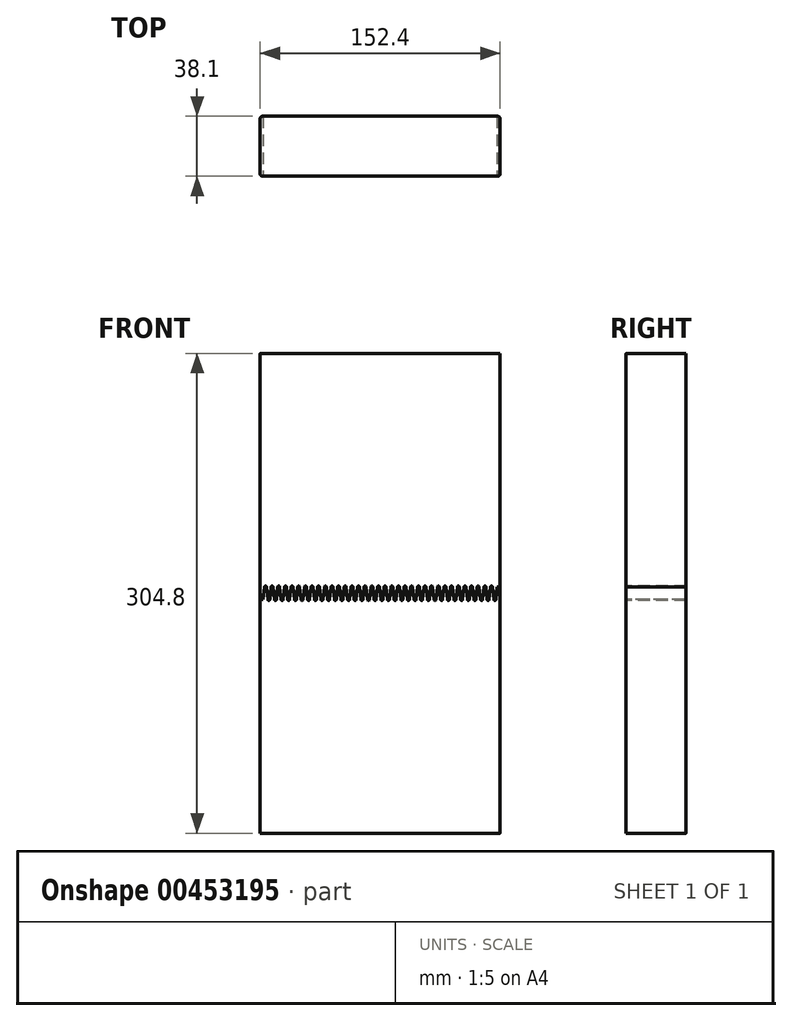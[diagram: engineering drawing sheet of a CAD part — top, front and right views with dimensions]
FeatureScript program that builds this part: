
annotation { "Feature Type Name" : "Feature", "Feature Type Description" : "" }
export const myFeature = defineFeature(function(context is Context, id is Id, definition is map)
    precondition{}
    {
        {
            var Q0;
            Q0=qCreatedBy(makeId("Front.planeOp"),FACE);
            var sketch = newSketch(context, id + "F0", { "sketchPlane" : qUnion([Q0])});
            skLineSegment(sketch, "E0.bottom", {"start": v(0, 0) * mm, "end": v(-152.4, 0) * mm});
            skLineSegment(sketch, "E0.top", {"start": v(0, 304.8) * mm, "end": v(-152.4, 304.8) * mm});
            skLineSegment(sketch, "E0.left", {"start": v(0, 0) * mm, "end": v(0, 304.8) * mm});
            skLineSegment(sketch, "E0.right", {"start": v(-152.4, 0) * mm, "end": v(-152.4, 304.8) * mm});
            skLineSegment(sketch, "E1", {"start": v(-152.4, 152.4) * mm, "end": v(0, 152.4) * mm, "construction": true});
            skArc(sketch, "E2.1.0.0", {"start": v(-148.4, 156.37) * mm, "mid": v(-149.03, 157) * mm, "end": v(-149.66, 156.37) * mm});
            skArc(sketch, "E2.2.0.0", {"start": v(-144.17, 156.37) * mm, "mid": v(-144.8, 157) * mm, "end": v(-145.44, 156.37) * mm});
            skLineSegment(sketch, "E2.direction1", {"start": v(-153.25, 156.37) * mm, "end": v(-152.14, 156.37) * mm, "construction": true});
            skArc(sketch, "E3.0.3.0", {"start": v(-139.95, 156.37) * mm, "mid": v(-140.58, 157) * mm, "end": v(-141.22, 156.37) * mm});
            skArc(sketch, "E3.0.4.0", {"start": v(-135.73, 156.37) * mm, "mid": v(-136.36, 157) * mm, "end": v(-137, 156.37) * mm});
            skArc(sketch, "E3.0.5.0", {"start": v(-131.5, 156.37) * mm, "mid": v(-132.14, 157) * mm, "end": v(-132.77, 156.37) * mm});
            skArc(sketch, "E3.0.6.0", {"start": v(-127.28, 156.37) * mm, "mid": v(-127.92, 157) * mm, "end": v(-128.55, 156.37) * mm});
            skArc(sketch, "E3.0.7.0", {"start": v(-123.06, 156.37) * mm, "mid": v(-123.7, 157) * mm, "end": v(-124.33, 156.37) * mm});
            skArc(sketch, "E3.0.8.0", {"start": v(-118.84, 156.37) * mm, "mid": v(-119.47, 157) * mm, "end": v(-120.1, 156.37) * mm});
            skArc(sketch, "E3.0.9.0", {"start": v(-114.61, 156.37) * mm, "mid": v(-115.25, 157) * mm, "end": v(-115.88, 156.37) * mm});
            skArc(sketch, "E3.0.10.0", {"start": v(-110.4, 156.37) * mm, "mid": v(-111.03, 157) * mm, "end": v(-111.66, 156.37) * mm});
            skArc(sketch, "E3.0.11.0", {"start": v(-106.17, 156.37) * mm, "mid": v(-106.8, 157) * mm, "end": v(-107.44, 156.37) * mm});
            skArc(sketch, "E3.0.12.0", {"start": v(-101.95, 156.37) * mm, "mid": v(-102.58, 157) * mm, "end": v(-103.22, 156.37) * mm});
            skArc(sketch, "E3.0.13.0", {"start": v(-97.72, 156.37) * mm, "mid": v(-98.36, 157) * mm, "end": v(-99, 156.37) * mm});
            skArc(sketch, "E3.0.14.0", {"start": v(-93.5, 156.37) * mm, "mid": v(-94.14, 157) * mm, "end": v(-94.77, 156.37) * mm});
            skArc(sketch, "E3.0.15.0", {"start": v(-89.28, 156.37) * mm, "mid": v(-89.91, 157) * mm, "end": v(-90.55, 156.37) * mm});
            skArc(sketch, "E3.0.16.0", {"start": v(-85.06, 156.37) * mm, "mid": v(-85.7, 157) * mm, "end": v(-86.33, 156.37) * mm});
            skArc(sketch, "E3.0.17.0", {"start": v(-80.83, 156.37) * mm, "mid": v(-81.47, 157) * mm, "end": v(-82.1, 156.37) * mm});
            skArc(sketch, "E3.0.18.0", {"start": v(-76.61, 156.37) * mm, "mid": v(-77.25, 157) * mm, "end": v(-77.88, 156.37) * mm});
            skArc(sketch, "E3.0.19.0", {"start": v(-72.39, 156.37) * mm, "mid": v(-73.02, 157) * mm, "end": v(-73.66, 156.37) * mm});
            skArc(sketch, "E3.0.20.0", {"start": v(-68.17, 156.37) * mm, "mid": v(-68.8, 157) * mm, "end": v(-69.44, 156.37) * mm});
            skArc(sketch, "E3.0.21.0", {"start": v(-63.94, 156.37) * mm, "mid": v(-64.58, 157) * mm, "end": v(-65.21, 156.37) * mm});
            skArc(sketch, "E3.0.22.0", {"start": v(-59.72, 156.37) * mm, "mid": v(-60.36, 157) * mm, "end": v(-61, 156.37) * mm});
            skArc(sketch, "E3.0.23.0", {"start": v(-55.5, 156.37) * mm, "mid": v(-56.13, 157) * mm, "end": v(-56.77, 156.37) * mm});
            skArc(sketch, "E3.0.24.0", {"start": v(-51.27, 156.37) * mm, "mid": v(-51.9, 157) * mm, "end": v(-52.54, 156.37) * mm});
            skArc(sketch, "E3.0.25.0", {"start": v(-47.05, 156.37) * mm, "mid": v(-47.69, 157) * mm, "end": v(-48.32, 156.37) * mm});
            skArc(sketch, "E3.0.26.0", {"start": v(-42.83, 156.37) * mm, "mid": v(-43.46, 157) * mm, "end": v(-44.1, 156.37) * mm});
            skArc(sketch, "E3.0.27.0", {"start": v(-38.6, 156.37) * mm, "mid": v(-39.24, 157) * mm, "end": v(-39.88, 156.37) * mm});
            skArc(sketch, "E3.0.28.0", {"start": v(-34.38, 156.37) * mm, "mid": v(-35.02, 157) * mm, "end": v(-35.65, 156.37) * mm});
            skArc(sketch, "E3.0.29.0", {"start": v(-30.16, 156.37) * mm, "mid": v(-30.8, 157) * mm, "end": v(-31.43, 156.37) * mm});
            skArc(sketch, "E4.0.30.0", {"start": v(-25.94, 156.37) * mm, "mid": v(-26.57, 157) * mm, "end": v(-27.2, 156.37) * mm});
            skArc(sketch, "E4.0.31.0", {"start": v(-21.72, 156.37) * mm, "mid": v(-22.35, 157) * mm, "end": v(-22.99, 156.37) * mm});
            skArc(sketch, "E4.0.32.0", {"start": v(-17.5, 156.37) * mm, "mid": v(-18.13, 157) * mm, "end": v(-18.76, 156.37) * mm});
            skArc(sketch, "E4.0.33.0", {"start": v(-13.27, 156.37) * mm, "mid": v(-13.87, 157) * mm, "end": v(-14.54, 156.44) * mm});
            skArc(sketch, "E4.0.34.0", {"start": v(-9.05, 156.37) * mm, "mid": v(-9.68, 157) * mm, "end": v(-10.32, 156.37) * mm});
            skArc(sketch, "E5.0.35.0", {"start": v(-4.83, 156.37) * mm, "mid": v(-5.46, 157) * mm, "end": v(-6.1, 156.37) * mm});
            skArc(sketch, "E6.1.0.0", {"start": v(-147.55, 148.43) * mm, "mid": v(-146.92, 147.8) * mm, "end": v(-146.28, 148.43) * mm});
            skArc(sketch, "E6.2.0.0", {"start": v(-143.33, 148.43) * mm, "mid": v(-142.7, 147.8) * mm, "end": v(-142.06, 148.43) * mm});
            skArc(sketch, "E6.3.0.0", {"start": v(-139.1, 148.43) * mm, "mid": v(-138.47, 147.8) * mm, "end": v(-137.84, 148.43) * mm});
            skArc(sketch, "E6.4.0.0", {"start": v(-134.88, 148.43) * mm, "mid": v(-134.25, 147.8) * mm, "end": v(-133.61, 148.43) * mm});
            skArc(sketch, "E6.5.0.0", {"start": v(-130.66, 148.43) * mm, "mid": v(-130.03, 147.8) * mm, "end": v(-129.4, 148.43) * mm});
            skArc(sketch, "E6.6.0.0", {"start": v(-126.44, 148.43) * mm, "mid": v(-125.8, 147.8) * mm, "end": v(-125.17, 148.43) * mm});
            skArc(sketch, "E6.7.0.0", {"start": v(-122.22, 148.43) * mm, "mid": v(-121.58, 147.8) * mm, "end": v(-120.95, 148.43) * mm});
            skArc(sketch, "E6.8.0.0", {"start": v(-118, 148.43) * mm, "mid": v(-117.36, 147.8) * mm, "end": v(-116.72, 148.43) * mm});
            skArc(sketch, "E6.9.0.0", {"start": v(-113.77, 148.43) * mm, "mid": v(-113.14, 147.8) * mm, "end": v(-112.5, 148.43) * mm});
            skArc(sketch, "E6.10.0.0", {"start": v(-109.55, 148.43) * mm, "mid": v(-108.91, 147.8) * mm, "end": v(-108.28, 148.43) * mm});
            skArc(sketch, "E6.11.0.0", {"start": v(-105.33, 148.43) * mm, "mid": v(-104.7, 147.8) * mm, "end": v(-104.06, 148.43) * mm});
            skArc(sketch, "E6.12.0.0", {"start": v(-101.1, 148.43) * mm, "mid": v(-100.47, 147.8) * mm, "end": v(-99.83, 148.43) * mm});
            skArc(sketch, "E6.13.0.0", {"start": v(-96.88, 148.43) * mm, "mid": v(-96.25, 147.8) * mm, "end": v(-95.61, 148.43) * mm});
            skArc(sketch, "E6.14.0.0", {"start": v(-92.66, 148.43) * mm, "mid": v(-92.02, 147.8) * mm, "end": v(-91.39, 148.43) * mm});
            skArc(sketch, "E6.15.0.0", {"start": v(-88.44, 148.43) * mm, "mid": v(-87.8, 147.8) * mm, "end": v(-87.17, 148.43) * mm});
            skArc(sketch, "E6.16.0.0", {"start": v(-84.21, 148.43) * mm, "mid": v(-83.58, 147.8) * mm, "end": v(-82.94, 148.43) * mm});
            skArc(sketch, "E6.17.0.0", {"start": v(-80, 148.43) * mm, "mid": v(-79.36, 147.8) * mm, "end": v(-78.72, 148.43) * mm});
            skArc(sketch, "E6.18.0.0", {"start": v(-75.77, 148.43) * mm, "mid": v(-75.13, 147.8) * mm, "end": v(-74.5, 148.43) * mm});
            skArc(sketch, "E6.19.0.0", {"start": v(-71.55, 148.43) * mm, "mid": v(-70.91, 147.8) * mm, "end": v(-70.28, 148.43) * mm});
            skArc(sketch, "E6.20.0.0", {"start": v(-67.32, 148.43) * mm, "mid": v(-66.69, 147.8) * mm, "end": v(-66.05, 148.43) * mm});
            skArc(sketch, "E6.21.0.0", {"start": v(-63.1, 148.43) * mm, "mid": v(-62.47, 147.8) * mm, "end": v(-61.83, 148.43) * mm});
            skArc(sketch, "E6.22.0.0", {"start": v(-58.88, 148.43) * mm, "mid": v(-58.24, 147.8) * mm, "end": v(-57.6, 148.43) * mm});
            skArc(sketch, "E6.23.0.0", {"start": v(-54.66, 148.43) * mm, "mid": v(-54.02, 147.8) * mm, "end": v(-53.39, 148.43) * mm});
            skArc(sketch, "E6.24.0.0", {"start": v(-50.43, 148.43) * mm, "mid": v(-49.8, 147.8) * mm, "end": v(-49.16, 148.43) * mm});
            skArc(sketch, "E6.25.0.0", {"start": v(-46.21, 148.43) * mm, "mid": v(-45.58, 147.8) * mm, "end": v(-44.94, 148.43) * mm});
            skArc(sketch, "E6.26.0.0", {"start": v(-41.99, 148.43) * mm, "mid": v(-41.35, 147.8) * mm, "end": v(-40.72, 148.43) * mm});
            skArc(sketch, "E6.27.0.0", {"start": v(-37.77, 148.43) * mm, "mid": v(-37.13, 147.8) * mm, "end": v(-36.5, 148.43) * mm});
            skArc(sketch, "E6.28.0.0", {"start": v(-33.54, 148.43) * mm, "mid": v(-32.9, 147.8) * mm, "end": v(-32.27, 148.43) * mm});
            skArc(sketch, "E6.29.0.0", {"start": v(-29.32, 148.43) * mm, "mid": v(-28.69, 147.8) * mm, "end": v(-28.05, 148.43) * mm});
            skArc(sketch, "E6.30.0.0", {"start": v(-25.1, 148.43) * mm, "mid": v(-24.46, 147.8) * mm, "end": v(-23.83, 148.43) * mm});
            skArc(sketch, "E6.31.0.0", {"start": v(-20.88, 148.43) * mm, "mid": v(-20.24, 147.8) * mm, "end": v(-19.6, 148.43) * mm});
            skArc(sketch, "E6.32.0.0", {"start": v(-16.65, 148.43) * mm, "mid": v(-16.02, 147.8) * mm, "end": v(-15.38, 148.43) * mm});
            skArc(sketch, "E6.33.0.0", {"start": v(-12.43, 148.43) * mm, "mid": v(-11.8, 147.8) * mm, "end": v(-11.16, 148.43) * mm});
            skArc(sketch, "E6.34.0.0", {"start": v(-8.2, 148.43) * mm, "mid": v(-7.57, 147.8) * mm, "end": v(-6.94, 148.43) * mm});
            skArc(sketch, "E6.35.0.0", {"start": v(-3.99, 148.43) * mm, "mid": v(-3.35, 147.8) * mm, "end": v(-2.72, 148.43) * mm});
            skLineSegment(sketch, "E7", {"start": v(-149.66, 156.44) * mm, "end": v(-150.5, 148.36) * mm});
            skLineSegment(sketch, "E8", {"start": v(-148.4, 156.44) * mm, "end": v(-147.55, 148.36) * mm});
            skLineSegment(sketch, "E9.1.0.0", {"start": v(-145.44, 156.44) * mm, "end": v(-146.29, 148.36) * mm});
            skLineSegment(sketch, "E9.2.0.0", {"start": v(-141.21, 156.44) * mm, "end": v(-142.06, 148.36) * mm});
            skLineSegment(sketch, "E9.3.0.0", {"start": v(-137, 156.44) * mm, "end": v(-137.84, 148.36) * mm});
            skLineSegment(sketch, "E9.4.0.0", {"start": v(-132.77, 156.44) * mm, "end": v(-133.62, 148.36) * mm});
            skLineSegment(sketch, "E9.5.0.0", {"start": v(-128.55, 156.44) * mm, "end": v(-129.4, 148.36) * mm});
            skLineSegment(sketch, "E9.6.0.0", {"start": v(-124.32, 156.44) * mm, "end": v(-125.17, 148.36) * mm});
            skLineSegment(sketch, "E9.7.0.0", {"start": v(-120.1, 156.44) * mm, "end": v(-120.95, 148.36) * mm});
            skLineSegment(sketch, "E9.8.0.0", {"start": v(-115.88, 156.44) * mm, "end": v(-116.73, 148.36) * mm});
            skLineSegment(sketch, "E9.9.0.0", {"start": v(-111.66, 156.44) * mm, "end": v(-112.5, 148.36) * mm});
            skLineSegment(sketch, "E9.10.0.0", {"start": v(-107.43, 156.44) * mm, "end": v(-108.28, 148.36) * mm});
            skLineSegment(sketch, "E9.11.0.0", {"start": v(-103.21, 156.44) * mm, "end": v(-104.06, 148.36) * mm});
            skLineSegment(sketch, "E9.12.0.0", {"start": v(-98.99, 156.44) * mm, "end": v(-99.84, 148.36) * mm});
            skLineSegment(sketch, "E9.13.0.0", {"start": v(-94.77, 156.44) * mm, "end": v(-95.61, 148.36) * mm});
            skLineSegment(sketch, "E9.14.0.0", {"start": v(-90.54, 156.44) * mm, "end": v(-91.4, 148.36) * mm});
            skLineSegment(sketch, "E9.15.0.0", {"start": v(-86.32, 156.44) * mm, "end": v(-87.17, 148.36) * mm});
            skLineSegment(sketch, "E9.16.0.0", {"start": v(-82.1, 156.44) * mm, "end": v(-82.95, 148.36) * mm});
            skLineSegment(sketch, "E9.17.0.0", {"start": v(-77.88, 156.44) * mm, "end": v(-78.72, 148.36) * mm});
            skLineSegment(sketch, "E9.18.0.0", {"start": v(-73.65, 156.44) * mm, "end": v(-74.5, 148.36) * mm});
            skLineSegment(sketch, "E9.19.0.0", {"start": v(-69.43, 156.44) * mm, "end": v(-70.28, 148.36) * mm});
            skLineSegment(sketch, "E9.20.0.0", {"start": v(-65.2, 156.44) * mm, "end": v(-66.06, 148.36) * mm});
            skLineSegment(sketch, "E9.21.0.0", {"start": v(-60.99, 156.44) * mm, "end": v(-61.83, 148.36) * mm});
            skLineSegment(sketch, "E9.22.0.0", {"start": v(-56.76, 156.44) * mm, "end": v(-57.61, 148.36) * mm});
            skLineSegment(sketch, "E9.23.0.0", {"start": v(-52.54, 156.44) * mm, "end": v(-53.39, 148.36) * mm});
            skLineSegment(sketch, "E9.24.0.0", {"start": v(-48.32, 156.44) * mm, "end": v(-49.17, 148.36) * mm});
            skLineSegment(sketch, "E9.25.0.0", {"start": v(-44.1, 156.44) * mm, "end": v(-44.94, 148.36) * mm});
            skLineSegment(sketch, "E9.26.0.0", {"start": v(-39.87, 156.44) * mm, "end": v(-40.72, 148.36) * mm});
            skLineSegment(sketch, "E9.27.0.0", {"start": v(-35.65, 156.44) * mm, "end": v(-36.5, 148.36) * mm});
            skLineSegment(sketch, "E9.28.0.0", {"start": v(-31.43, 156.44) * mm, "end": v(-32.28, 148.36) * mm});
            skLineSegment(sketch, "E9.29.0.0", {"start": v(-27.2, 156.44) * mm, "end": v(-28.05, 148.36) * mm});
            skLineSegment(sketch, "E9.30.0.0", {"start": v(-22.98, 156.44) * mm, "end": v(-23.83, 148.36) * mm});
            skLineSegment(sketch, "E9.31.0.0", {"start": v(-18.76, 156.44) * mm, "end": v(-19.6, 148.36) * mm});
            skLineSegment(sketch, "E9.32.0.0", {"start": v(-14.54, 156.44) * mm, "end": v(-15.39, 148.36) * mm});
            skLineSegment(sketch, "E9.33.0.0", {"start": v(-10.32, 156.44) * mm, "end": v(-11.16, 148.36) * mm});
            skLineSegment(sketch, "E9.34.0.0", {"start": v(-6.1, 156.44) * mm, "end": v(-6.94, 148.36) * mm});
            skLineSegment(sketch, "E9.35.0.0", {"start": v(-1.87, 156.44) * mm, "end": v(-2.72, 148.36) * mm});
            skLineSegment(sketch, "E10.1.0.0", {"start": v(-144.17, 156.44) * mm, "end": v(-143.33, 148.36) * mm});
            skLineSegment(sketch, "E10.2.0.0", {"start": v(-139.95, 156.44) * mm, "end": v(-139.1, 148.36) * mm});
            skLineSegment(sketch, "E10.3.0.0", {"start": v(-135.73, 156.44) * mm, "end": v(-134.88, 148.36) * mm});
            skLineSegment(sketch, "E10.4.0.0", {"start": v(-131.5, 156.44) * mm, "end": v(-130.66, 148.36) * mm});
            skLineSegment(sketch, "E10.5.0.0", {"start": v(-127.28, 156.44) * mm, "end": v(-126.44, 148.36) * mm});
            skLineSegment(sketch, "E10.6.0.0", {"start": v(-123.06, 156.44) * mm, "end": v(-122.21, 148.36) * mm});
            skLineSegment(sketch, "E10.7.0.0", {"start": v(-118.84, 156.44) * mm, "end": v(-118, 148.36) * mm});
            skLineSegment(sketch, "E10.8.0.0", {"start": v(-114.62, 156.44) * mm, "end": v(-113.77, 148.36) * mm});
            skLineSegment(sketch, "E10.9.0.0", {"start": v(-110.4, 156.44) * mm, "end": v(-109.55, 148.36) * mm});
            skLineSegment(sketch, "E10.10.0.0", {"start": v(-106.17, 156.44) * mm, "end": v(-105.32, 148.36) * mm});
            skLineSegment(sketch, "E10.11.0.0", {"start": v(-101.95, 156.44) * mm, "end": v(-101.1, 148.36) * mm});
            skLineSegment(sketch, "E10.12.0.0", {"start": v(-97.73, 156.44) * mm, "end": v(-96.88, 148.36) * mm});
            skLineSegment(sketch, "E10.13.0.0", {"start": v(-93.5, 156.44) * mm, "end": v(-92.66, 148.36) * mm});
            skLineSegment(sketch, "E10.14.0.0", {"start": v(-89.28, 156.44) * mm, "end": v(-88.43, 148.36) * mm});
            skLineSegment(sketch, "E10.15.0.0", {"start": v(-85.06, 156.44) * mm, "end": v(-84.21, 148.36) * mm});
            skLineSegment(sketch, "E10.16.0.0", {"start": v(-80.84, 156.44) * mm, "end": v(-79.99, 148.36) * mm});
            skLineSegment(sketch, "E10.17.0.0", {"start": v(-76.61, 156.44) * mm, "end": v(-75.77, 148.36) * mm});
            skLineSegment(sketch, "E10.18.0.0", {"start": v(-72.4, 156.44) * mm, "end": v(-71.54, 148.36) * mm});
            skLineSegment(sketch, "E10.19.0.0", {"start": v(-68.17, 156.44) * mm, "end": v(-67.32, 148.36) * mm});
            skLineSegment(sketch, "E10.20.0.0", {"start": v(-63.95, 156.44) * mm, "end": v(-63.1, 148.36) * mm});
            skLineSegment(sketch, "E10.21.0.0", {"start": v(-59.72, 156.44) * mm, "end": v(-58.88, 148.36) * mm});
            skLineSegment(sketch, "E10.22.0.0", {"start": v(-55.5, 156.44) * mm, "end": v(-54.65, 148.36) * mm});
            skLineSegment(sketch, "E10.23.0.0", {"start": v(-51.28, 156.44) * mm, "end": v(-50.43, 148.36) * mm});
            skLineSegment(sketch, "E10.24.0.0", {"start": v(-47.06, 156.44) * mm, "end": v(-46.2, 148.36) * mm});
            skLineSegment(sketch, "E10.25.0.0", {"start": v(-42.83, 156.44) * mm, "end": v(-41.99, 148.36) * mm});
            skLineSegment(sketch, "E10.26.0.0", {"start": v(-38.61, 156.44) * mm, "end": v(-37.76, 148.36) * mm});
            skLineSegment(sketch, "E10.27.0.0", {"start": v(-34.39, 156.44) * mm, "end": v(-33.54, 148.36) * mm});
            skLineSegment(sketch, "E10.28.0.0", {"start": v(-30.17, 156.44) * mm, "end": v(-29.32, 148.36) * mm});
            skLineSegment(sketch, "E10.29.0.0", {"start": v(-25.94, 156.44) * mm, "end": v(-25.1, 148.36) * mm});
            skLineSegment(sketch, "E10.30.0.0", {"start": v(-21.72, 156.44) * mm, "end": v(-20.87, 148.36) * mm});
            skLineSegment(sketch, "E10.31.0.0", {"start": v(-17.5, 156.44) * mm, "end": v(-16.65, 148.36) * mm});
            skLineSegment(sketch, "E10.32.0.0", {"start": v(-13.28, 156.44) * mm, "end": v(-12.43, 148.36) * mm});
            skLineSegment(sketch, "E10.33.0.0", {"start": v(-9.05, 156.44) * mm, "end": v(-8.2, 148.36) * mm});
            skLineSegment(sketch, "E10.34.0.0", {"start": v(-4.83, 156.44) * mm, "end": v(-3.98, 148.36) * mm});
            skLineSegment(sketch, "E11", {"start": v(-150.5, 148.36) * mm, "end": v(-152.4, 148.36) * mm});
            skLineSegment(sketch, "E12", {"start": v(-1.87, 156.44) * mm, "end": v(0, 156.44) * mm});
            skLineSegment(sketch, "E13.trimOffspring", {"start": v(0.23, 148.43) * mm, "end": v(0.24, 148.43) * mm});
            skLineSegment(sketch, "E14.trimOffspring", {"start": v(-0.6, 156.37) * mm, "end": v(-0.6, 156.37) * mm});
            skLineSegment(sketch, "E15.trimOffspring", {"start": v(-149.67, 156.37) * mm, "end": v(-149.03, 156.37) * mm, "construction": true});
            skSolve(sketch);
        }
        {
            var Q0;
            {var subQ104=sQuery(id+"F0.wireOp",EDGE,"E0.top");Q0=makeQuery(id+"F0.imprint","IMPRINT",FACE,{"disambiguationData":[TD([[makeQuery(id+"F0.imprint","IMPRINT",EDGE,{"derivedFrom":subQ104}),1.0]])]});}
            extrude(context, id + "F1", {"entities" : qUnion([Q0]), "oppositeDirection" : true, "depth" : 38.1 * mm});
        }
        {
            var Q0;
            {var subQ105=sQuery(id+"F0.wireOp",EDGE,"E0.bottom");Q0=makeQuery(id+"F0.imprint","IMPRINT",FACE,{"disambiguationData":[TD([[makeQuery(id+"F0.imprint","IMPRINT",EDGE,{"derivedFrom":subQ105}),-1.0]])]});}
            extrude(context, id + "F2", {"entities" : qUnion([Q0]), "oppositeDirection" : true, "depth" : 38.1 * mm});
        }
        {
            var Q0;
            Q0=makeQuery(id+"F1.opExtrude","CAP_EDGE",EDGE,{"disambiguationData":[OSD([sQuery(id+"F0.wireOp",EDGE,"E0.left")])],"isStart":true});
            var Q1;
            Q1=makeQuery(id+"F2.opExtrude","CAP_EDGE",EDGE,{"disambiguationData":[OSD([sQuery(id+"F0.wireOp",EDGE,"E0.left")])],"isStart":true});
            var Q2;
            Q2=makeQuery(id+"F1.opExtrude","CAP_EDGE",EDGE,{"disambiguationData":[OSD([sQuery(id+"F0.wireOp",EDGE,"E0.left")])],"isStart":false});
            var Q3;
            Q3=makeQuery(id+"F2.opExtrude","CAP_EDGE",EDGE,{"disambiguationData":[OSD([sQuery(id+"F0.wireOp",EDGE,"E0.left")])],"isStart":false});
            var Q4;
            Q4=makeQuery(id+"F2.opExtrude","CAP_EDGE",EDGE,{"disambiguationData":[OSD([sQuery(id+"F0.wireOp",EDGE,"E0.right")])],"isStart":false});
            var Q5;
            Q5=makeQuery(id+"F1.opExtrude","CAP_EDGE",EDGE,{"disambiguationData":[OSD([sQuery(id+"F0.wireOp",EDGE,"E0.right")])],"isStart":false});
            var Q6;
            Q6=makeQuery(id+"F1.opExtrude","CAP_EDGE",EDGE,{"disambiguationData":[OSD([sQuery(id+"F0.wireOp",EDGE,"E0.right")])],"isStart":true});
            var Q7;
            Q7=makeQuery(id+"F2.opExtrude","CAP_EDGE",EDGE,{"disambiguationData":[OSD([sQuery(id+"F0.wireOp",EDGE,"E0.right")])],"isStart":true});
            fillet(context, id + "F3", {"entities" : qUnion([Q0, Q1, Q2, Q3, Q4, Q5, Q6, Q7]), "radius" : 1.59 * mm, "tangentPropagation" : true, "allowEdgeOverflow" : false});
        }
    });
